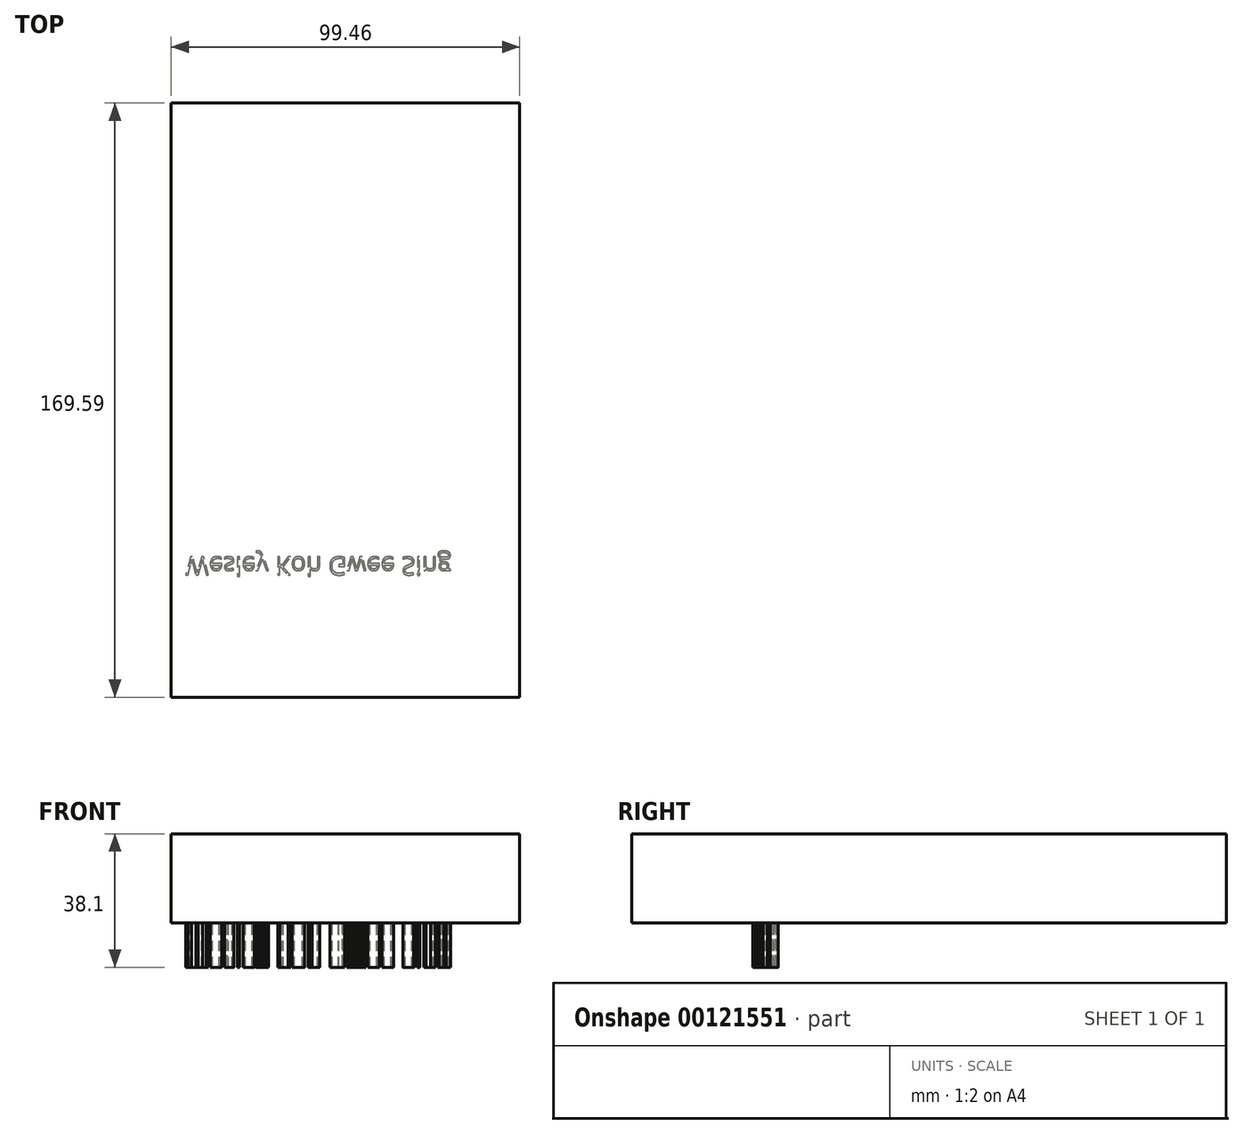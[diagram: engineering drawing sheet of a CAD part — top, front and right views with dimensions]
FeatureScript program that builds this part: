
annotation { "Feature Type Name" : "Feature", "Feature Type Description" : "" }
export const myFeature = defineFeature(function(context is Context, id is Id, definition is map)
    precondition{}
    {
        {
            var Q0;
            Q0=qCreatedBy(makeId("Top.planeOp"),FACE);
            var sketch = newSketch(context, id + "F0", { "sketchPlane" : qUnion([Q0])});
            skLineSegment(sketch, "E0.bottom", {"start": v(-49.73, -88.82) * mm, "end": v(49.73, -88.82) * mm});
            skLineSegment(sketch, "E0.top", {"start": v(-49.73, 80.77) * mm, "end": v(49.73, 80.77) * mm});
            skLineSegment(sketch, "E0.left", {"start": v(-49.73, -88.82) * mm, "end": v(-49.73, 80.77) * mm});
            skLineSegment(sketch, "E0.right", {"start": v(49.73, -88.82) * mm, "end": v(49.73, 80.77) * mm});
            skPoint(sketch, "E0.middle", {"position": v(0, -4.03) * mm});
            skSolve(sketch);
        }
        {
            var Q0;
            Q0=makeQuery(id+"F0.imprint","IMPRINT",FACE,{"disambiguationData":[TD([[makeQuery(id+"F0.imprint","IMPRINT",EDGE,{"derivedFrom":sQuery(id+"F0.wireOp",EDGE,"E0.bottom")}),1.0]])]});
            extrude(context, id + "F1", {"entities" : qUnion([Q0]), "depth" : 25.4 * mm});
        }
        {
            var Q0;
            Q0=makeQuery(id+"F1.opExtrude","CAP_FACE",FACE,{"disambiguationData":[OSD([sQuery(id+"F0.wireOp",EDGE,"E0.bottom"),sQuery(id+"F0.wireOp",EDGE,"E0.top"),sQuery(id+"F0.wireOp",EDGE,"E0.left"),sQuery(id+"F0.wireOp",EDGE,"E0.right")])],"isStart":true});
            var sketch = newSketch(context, id + "F2", { "sketchPlane" : qUnion([Q0])});
            skText(sketch, "E1", { "text": "Wesley Koh Gwee Sing\n\n", "fontName": "OpenSans-Regular.ttf"});
            const initialGuessF2  = {"E1": [-0.04568, 0.0488, 1, 0, 0.00521]};
            skSetInitialGuess(sketch, initialGuessF2);
            skSolve(sketch);
        }
        {
            var Q0;
            Q0 = qSketchRegion(id + "F2", true);
            extrude(context, id + "F3", {"entities" : qUnion([Q0]), "operationType" : NewBodyOperationType.ADD, "depth" : 12.7 * mm});
        }
    });
